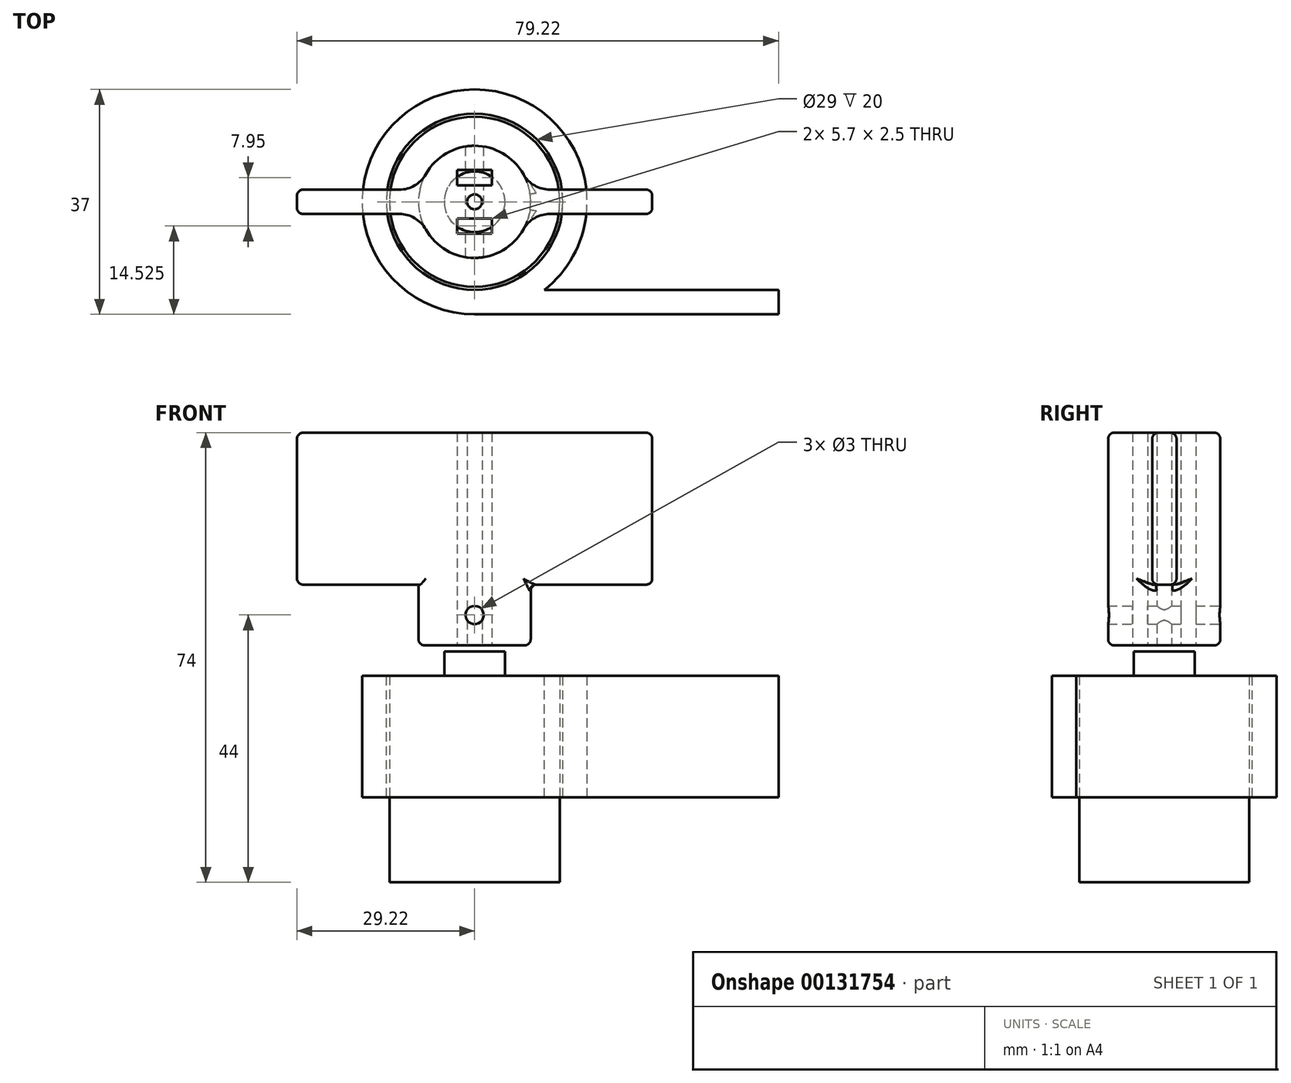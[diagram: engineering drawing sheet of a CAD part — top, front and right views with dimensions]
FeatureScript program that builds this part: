
annotation { "Feature Type Name" : "Feature", "Feature Type Description" : "" }
export const myFeature = defineFeature(function(context is Context, id is Id, definition is map)
    precondition{}
    {
        {
            assignVariable(context, id + "F0", {"name" : "paddleWidth", "anyValue" : 25});
        }
        {
            assignVariable(context, id + "F1", {"name" : "pCount", "anyValue" : 2});
        }
        {
            var Q0;
            Q0=qCreatedBy(makeId("Top.planeOp"),FACE);
            var sketch = newSketch(context, id + "F2", { "sketchPlane" : qUnion([Q0])});
            skCircle(sketch, "E0", {"center": v(0, 0) * mm, "radius": 9.23 * mm});
            skCircle(sketch, "E1", {"center": v(0, 0) * mm, "radius": 1.23 * mm});
            skLineSegment(sketch, "E2.bottom", {"start": v(-2.85, 5.23) * mm, "end": v(2.85, 5.23) * mm});
            skLineSegment(sketch, "E2.top", {"start": v(-2.85, 2.73) * mm, "end": v(2.85, 2.73) * mm});
            skLineSegment(sketch, "E2.left", {"start": v(-2.85, 5.23) * mm, "end": v(-2.85, 2.73) * mm});
            skLineSegment(sketch, "E2.right", {"start": v(2.85, 5.23) * mm, "end": v(2.85, 2.73) * mm});
            skPoint(sketch, "E2.middle", {"position": v(0, 3.98) * mm});
            skLineSegment(sketch, "E3", {"start": v(-9, 2) * mm, "end": v(-29.22, 2) * mm});
            skLineSegment(sketch, "E4", {"start": v(-29.22, 2) * mm, "end": v(-29.22, -2) * mm});
            skLineSegment(sketch, "E5", {"start": v(-29.22, -2) * mm, "end": v(-9, -2) * mm});
            skPoint(sketch, "E6", {"position": v(-29.22, 0) * mm});
            skLineSegment(sketch, "E7.1.0", {"start": v(2.85, -5.23) * mm, "end": v(-2.85, -5.23) * mm});
            skLineSegment(sketch, "E7.1.1", {"start": v(2.85, -5.23) * mm, "end": v(2.85, -2.72) * mm});
            skLineSegment(sketch, "E7.1.2", {"start": v(-2.85, -5.23) * mm, "end": v(-2.85, -2.73) * mm});
            skPoint(sketch, "E7.1.3", {"position": v(0, -3.98) * mm});
            skLineSegment(sketch, "E7.1.4", {"start": v(2.85, -2.72) * mm, "end": v(-2.85, -2.73) * mm});
            skSolve(sketch);
        }
        {
            var Q0;
            {var subQ0=sQuery(id+"F2.wireOp",EDGE,"E3");Q0=makeQuery(id+"F2.imprint","IMPRINT",FACE,{"disambiguationData":[TD([[makeQuery(id+"F2.imprint","IMPRINT",EDGE,{"derivedFrom":subQ0}),1.0]])]});}
            var Q1;
            Q1=makeQuery(id+"F2.imprint","IMPRINT",FACE,{"disambiguationData":[TD([[makeQuery(id+"F2.imprint","IMPRINT",EDGE,{"derivedFrom":sQuery(id+"F2.wireOp",EDGE,"E1")}),-1.0]])]});
            var Q2;
            Q2=makeQuery(id+"F2.imprint","IMPRINT",FACE,{"disambiguationData":[TD([[makeQuery(id+"F2.imprint","IMPRINT",EDGE,{"derivedFrom":sQuery(id+"F2.wireOp",EDGE,"E2.bottom")}),1.0]])]});
            var Q3;
            {var subQ0=sQuery(id+"F2.wireOp",EDGE,"24c3ac2a-dec3-4280-a04e-4fa5a5947572.1.4");Q3=makeQuery(id+"F2.imprint","IMPRINT",FACE,{"disambiguationData":[TD([[makeQuery(id+"F2.imprint","IMPRINT",EDGE,{"derivedFrom":subQ0}),1.0]])]});}
            extrude(context, id + "F3", {"entities" : qUnion([Q0, Q1, Q2, Q3]), "depth" : (getVariable(context, 'paddleWidth')) * mm});
        }
        {
            var Q0;
            Q0=makeQuery(id+"F3.opExtrude","SWEPT_EDGE",EDGE,{"disambiguationData":[OSD([sQuery(id+"F2.wireOp",EDGE,"E0"),sQuery(id+"F2.wireOp",EDGE,"E3")])]});
            var Q1;
            Q1=makeQuery(id+"F3.opExtrude","SWEPT_EDGE",EDGE,{"disambiguationData":[OSD([sQuery(id+"F2.wireOp",EDGE,"E0"),sQuery(id+"F2.wireOp",EDGE,"E5")])]});
            fillet(context, id + "F4", {"entities" : qUnion([Q0, Q1]), "radius" : 5 * mm, "tangentPropagation" : true, "allowEdgeOverflow" : false});
        }
        {
            var Q0;
            Q0=makeQuery(id+"F3.opExtrude","SWEPT_BODY",BODY,{"disambiguationData":[OSD([sQuery(id+"F2.wireOp",EDGE,"E0"),sQuery(id+"F2.wireOp",EDGE,"E1"),sQuery(id+"F2.wireOp",EDGE,"E2.bottom"),sQuery(id+"F2.wireOp",EDGE,"E2.top"),sQuery(id+"F2.wireOp",EDGE,"E2.left"),sQuery(id+"F2.wireOp",EDGE,"E2.right"),sQuery(id+"F2.wireOp",EDGE,"E3"),sQuery(id+"F2.wireOp",EDGE,"E4"),sQuery(id+"F2.wireOp",EDGE,"E5")])]});
            var Q1;
            Q1=makeQuery(id+"F3.opExtrude","SWEPT_FACE",FACE,{"disambiguationData":[OSD([sQuery(id+"F2.wireOp",EDGE,"E1")])]});
            circularPattern(context, id + "F5", {"operationType" : NewBodyOperationType.ADD, "entities" : qUnion([Q0]), "axis" : qUnion([Q1]), "angle" : (360 / getVariable(context, 'pCount')) * degree, "instanceCount" : 2});
        }
        {
            var Q0;
            Q0=makeQuery(id+"F2.imprint","IMPRINT",FACE,{"disambiguationData":[TD([[makeQuery(id+"F2.imprint","IMPRINT",EDGE,{"derivedFrom":sQuery(id+"F2.wireOp",EDGE,"E1")}),-1.0]])]});
            extrude(context, id + "F6", {"entities" : qUnion([Q0]), "operationType" : NewBodyOperationType.ADD, "oppositeDirection" : true, "depth" : 10 * mm});
        }
        {
            var Q0;
            Q0=makeQuery(id+"F3.opExtrude","CAP_EDGE",EDGE,{"disambiguationData":[OSD([sQuery(id+"F2.wireOp",EDGE,"E3")])],"isStart":true});
            var Q1;
            Q1=makeQuery(id+"F3.opExtrude","SWEPT_EDGE",EDGE,{"disambiguationData":[OSD([sQuery(id+"F2.wireOp",EDGE,"E3"),sQuery(id+"F2.wireOp",EDGE,"E4")])]});
            var Q2;
            Q2=makeQuery(id+"F3.opExtrude","CAP_EDGE",EDGE,{"disambiguationData":[OSD([sQuery(id+"F2.wireOp",EDGE,"E3")])],"isStart":false});
            var Q3;
            Q3=makeQuery(id+"F3.opExtrude","CAP_EDGE",EDGE,{"disambiguationData":[OSD([sQuery(id+"F2.wireOp",EDGE,"E5")])],"isStart":false});
            var Q4;
            Q4=makeQuery(id+"F3.opExtrude","SWEPT_EDGE",EDGE,{"disambiguationData":[OSD([sQuery(id+"F2.wireOp",EDGE,"E4"),sQuery(id+"F2.wireOp",EDGE,"E5")])]});
            var Q5;
            Q5=makeQuery(id+"F3.opExtrude","CAP_EDGE",EDGE,{"disambiguationData":[OSD([sQuery(id+"F2.wireOp",EDGE,"E5")])],"isStart":true});
            var Q6;
            Q6=makeQuery(id+"F3.opExtrude","CAP_EDGE",EDGE,{"disambiguationData":[OSD([sQuery(id+"F2.wireOp",EDGE,"E4")])],"isStart":false});
            var Q7;
            Q7=makeQuery(id+"F3.opExtrude","CAP_EDGE",EDGE,{"disambiguationData":[OSD([sQuery(id+"F2.wireOp",EDGE,"E4")])],"isStart":true});
            var Q8;
            Q8=makeQuery(id+"F5.opPattern","COPY",FACE,{"derivedFrom":makeQuery(id+"F3.opExtrude","SWEPT_FACE",FACE,{"disambiguationData":[OSD([sQuery(id+"F2.wireOp",EDGE,"E4")])]}),"instanceName":"1"});
            var Q9;
            {var subQ0=sQuery(id+"F2.wireOp",EDGE,"E5");var subQ1=sQuery(id+"F2.wireOp",EDGE,"E0");var subQ2=sQuery(id+"F2.wireOp",EDGE,"E3");var subQ3=sQuery(id+"F2.wireOp",EDGE,"E4");var subQ4=makeQuery(id+"F3.opExtrude","CAP_FACE",FACE,{"disambiguationData":[OSD([subQ1,sQuery(id+"F2.wireOp",EDGE,"E1"),sQuery(id+"F2.wireOp",EDGE,"E2.bottom"),sQuery(id+"F2.wireOp",EDGE,"E2.top"),sQuery(id+"F2.wireOp",EDGE,"E2.left"),sQuery(id+"F2.wireOp",EDGE,"E2.right"),subQ2,subQ3,subQ0,sQuery(id+"F2.wireOp",EDGE,"E7.1.0"),sQuery(id+"F2.wireOp",EDGE,"E7.1.1"),sQuery(id+"F2.wireOp",EDGE,"E7.1.2"),sQuery(id+"F2.wireOp",EDGE,"E7.1.4")])],"isStart":true});Q9=makeQuery(id+"F6.boolean.opBoolean","SPLIT",FACE,{"disambiguationData":[TD([makeQuery(id+"F5.opPattern","COPY",FACE,{"derivedFrom":makeQuery(id+"F3.opExtrude","SWEPT_FACE",FACE,{"disambiguationData":[OSD([subQ3])]}),"instanceName":"1"})])],"derivedFrom":makeQuery(id+"F5.boolean.opBoolean","MERGE",FACE,{"derivedFrom":[subQ4,makeQuery(id+"F5.opPattern","COPY",FACE,{"derivedFrom":subQ4,"instanceName":"1"})]})});}
            var Q10;
            Q10=makeQuery(id+"F6.opExtrude","CAP_EDGE",EDGE,{"disambiguationData":[OSD([sQuery(id+"F2.wireOp",EDGE,"E0")])],"isStart":false});
            fillet(context, id + "F7", {"entities" : qUnion([Q0, Q1, Q2, Q3, Q4, Q5, Q6, Q7, Q8, Q9, Q10]), "radius" : 1 * mm, "tangentPropagation" : true, "allowEdgeOverflow" : false});
        }
        {
            var Q0;
            Q0=qCreatedBy(makeId("Front.planeOp"),FACE);
            var sketch = newSketch(context, id + "F8", { "sketchPlane" : qUnion([Q0])});
            skLineSegment(sketch, "E8", {"start": v(0, -11) * mm, "end": v(5, -11) * mm});
            skLineSegment(sketch, "E9", {"start": v(5, -11) * mm, "end": v(5, -15) * mm});
            skLineSegment(sketch, "E10", {"start": v(5, -15) * mm, "end": v(14, -15) * mm});
            skLineSegment(sketch, "E11", {"start": v(14, -15) * mm, "end": v(14, -49) * mm});
            skLineSegment(sketch, "E12", {"start": v(14, -49) * mm, "end": v(0, -49) * mm});
            skLineSegment(sketch, "E13", {"start": v(0, -49) * mm, "end": v(0, -11) * mm});
            skSolve(sketch);
        }
        {
            var Q0;
            Q0=makeQuery(id+"F8.imprint","IMPRINT",FACE,{"disambiguationData":[TD([[makeQuery(id+"F8.imprint","IMPRINT",EDGE,{"derivedFrom":sQuery(id+"F8.wireOp",EDGE,"E8")}),-1.0]])]});
            var Q1;
            Q1=sQuery(id+"F8.wireOp",EDGE,"E13");
            revolve(context, id + "F9", {"entities" : qUnion([Q0]), "axis" : qUnion([Q1]), "revolveType" : RevolveType.FULL});
        }
        {
            var Q0;
            Q0=makeQuery(id+"F9.opRevolve","SWEPT_FACE",FACE,{"disambiguationData":[OSD([sQuery(id+"F8.wireOp",EDGE,"E10")])]});
            var sketch = newSketch(context, id + "F10", { "sketchPlane" : qUnion([Q0])});
            skCircle(sketch, "E14", {"center": v(0, 0) * mm, "radius": 14.5 * mm});
            skCircle(sketch, "E15", {"center": v(0, 0) * mm, "radius": 18.5 * mm});
            skLineSegment(sketch, "E16", {"start": v(0, -18.5) * mm, "end": v(50, -18.5) * mm});
            skLineSegment(sketch, "E17", {"start": v(50, -18.5) * mm, "end": v(50, -14.5) * mm});
            skLineSegment(sketch, "E18", {"start": v(50, -14.5) * mm, "end": v(11.49, -14.5) * mm});
            skSolve(sketch);
        }
        {
            var Q0;
            Q0=makeQuery(id+"F10.imprint","IMPRINT",FACE,{"disambiguationData":[TD([[makeQuery(id+"F10.imprint","IMPRINT",EDGE,{"derivedFrom":sQuery(id+"F10.wireOp",EDGE,"E14")}),-1.0]])]});
            var Q1;
            {var subQ0=sQuery(id+"F10.wireOp",EDGE,"E16");Q1=makeQuery(id+"F10.imprint","IMPRINT",FACE,{"disambiguationData":[TD([[makeQuery(id+"F10.imprint","IMPRINT",EDGE,{"derivedFrom":subQ0}),1.0]])]});}
            extrude(context, id + "F11", {"entities" : qUnion([Q0, Q1]), "oppositeDirection" : true, "depth" : 20 * mm});
        }
        {
            var Q0;
            {var subQ0=sQuery(id+"F2.wireOp",EDGE,"E2.top");Q0=makeQuery(id+"F6.boolean.opBoolean","MERGE",FACE,{"derivedFrom":[makeQuery(id+"F3.opExtrude","SWEPT_FACE",FACE,{"disambiguationData":[OSD([subQ0])]}),makeQuery(id+"F6.opExtrude","SWEPT_FACE",FACE,{"disambiguationData":[OSD([subQ0])]})]});}
            var sketch = newSketch(context, id + "F12", { "sketchPlane" : qUnion([Q0])});
            skCircle(sketch, "E19", {"center": v(0, -5) * mm, "radius": 1.5 * mm});
            skPoint(sketch, "E19.centerSnap0", {"position": v(0, 25) * mm});
            skSolve(sketch);
        }
        {
            var Q0;
            Q0=makeQuery(id+"F12.imprint","IMPRINT",FACE,{"disambiguationData":[TD([[makeQuery(id+"F12.imprint","IMPRINT",EDGE,{"derivedFrom":sQuery(id+"F12.wireOp",EDGE,"E19")}),1.0]])]});
            extrude(context, id + "F13", {"entities" : qUnion([Q0]), "operationType" : NewBodyOperationType.REMOVE, "oppositeDirection" : true, "depth" : 25 * mm, "hasSecondDirection" : true, "secondDirectionOppositeDirection" : false, "secondDirectionDepth" : 25 * mm});
        }
    });
